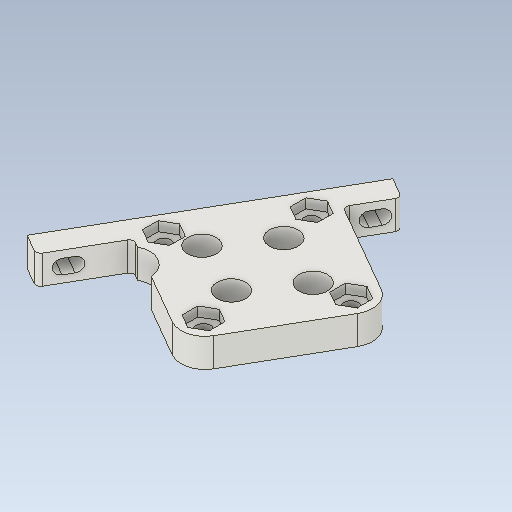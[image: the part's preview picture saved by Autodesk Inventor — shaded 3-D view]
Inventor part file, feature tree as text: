
AUTODESK INVENTOR PART (.ipt)
format: ipt  version: 2020.2 (Build 242310000, 310)  size: 161,280 bytes
history: imported  units: mm
features: imported_body x1
ambient origin geometry x8: Origin, YZ Plane, XZ Plane, XY Plane, X Axis, Y Axis, Z Axis, Center Point
bodies: Solide1 (imported_parasolid), Body3 (imported_parasolid)
feature tree (1):
  imported_body  NMx_Import_Brep_tag  [imported B-rep: ~62 faces, bbox_mm=[48.712813, 6.0, 50.497423]]
